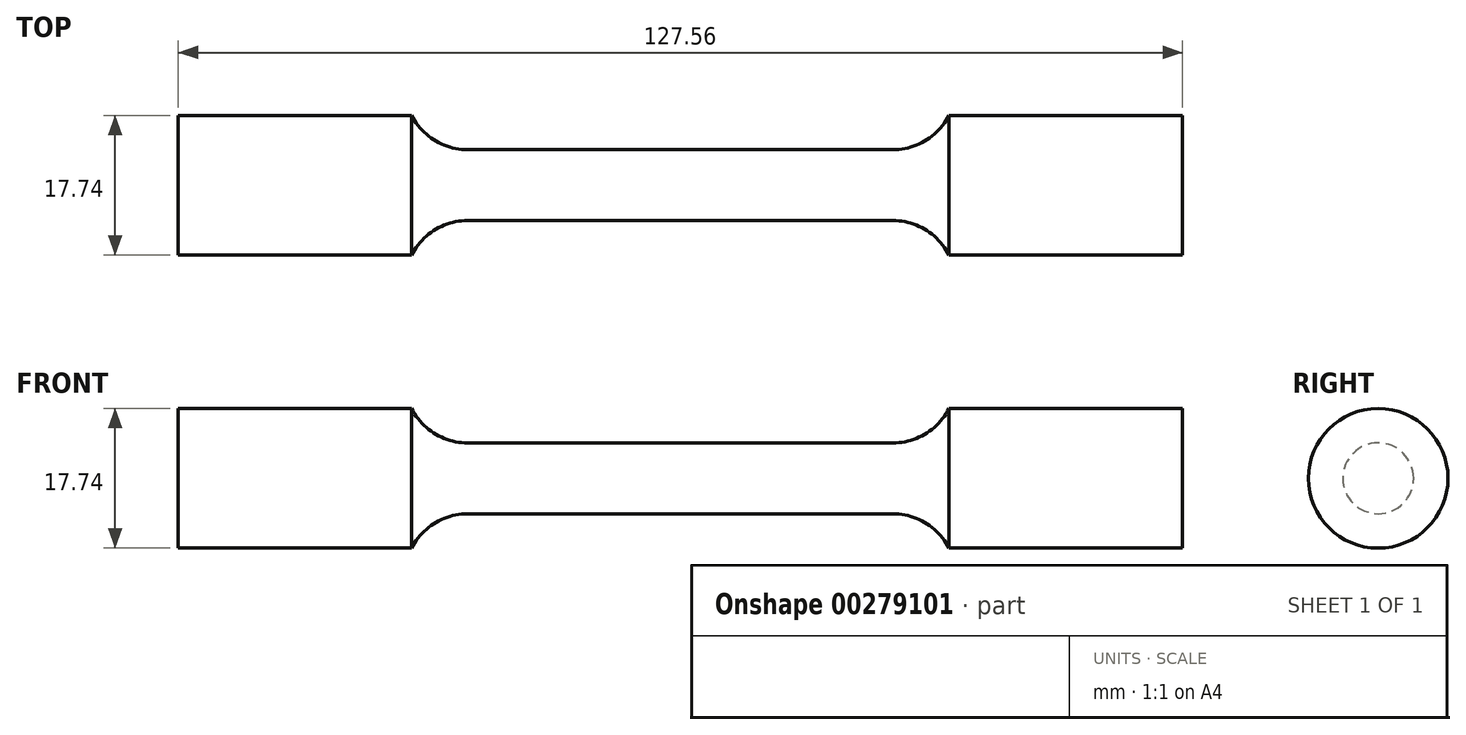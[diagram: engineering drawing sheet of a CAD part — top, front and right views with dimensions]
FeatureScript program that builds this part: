
annotation { "Feature Type Name" : "Feature", "Feature Type Description" : "" }
export const myFeature = defineFeature(function(context is Context, id is Id, definition is map)
    precondition{}
    {
        {
            var Q0;
            Q0=qCreatedBy(makeId("Front.planeOp"),FACE);
            var sketch = newSketch(context, id + "F0", { "sketchPlane" : qUnion([Q0])});
            skLineSegment(sketch, "E0", {"start": v(0, 4.5) * mm, "end": v(27, 4.5) * mm});
            skArc(sketch, "E1", {"start": v(27, 4.5) * mm, "mid": v(31.18, 5.68) * mm, "end": v(34.13, 8.87) * mm});
            skLineSegment(sketch, "E2", {"start": v(34.13, 8.87) * mm, "end": v(63.78, 8.87) * mm});
            skLineSegment(sketch, "E3", {"start": v(63.78, 8.87) * mm, "end": v(63.78, 0) * mm});
            skLineSegment(sketch, "E4.MirrorCS", {"start": v(0, 4.5) * mm, "end": v(-27, 4.5) * mm});
            skLineSegment(sketch, "E5.MirrorCS", {"start": v(-63.78, 8.87) * mm, "end": v(-63.78, 0) * mm});
            skLineSegment(sketch, "E6.MirrorCS", {"start": v(-34.13, 8.87) * mm, "end": v(-63.78, 8.87) * mm});
            skArc(sketch, "E7.MirrorCS", {"start": v(-27, 4.5) * mm, "mid": v(-31.18, 5.68) * mm, "end": v(-34.13, 8.87) * mm});
            skLineSegment(sketch, "E8", {"start": v(-63.78, 0) * mm, "end": v(63.78, 0) * mm});
            skLineSegment(sketch, "E9", {"start": v(-27, 4.5) * mm, "end": v(27, 4.5) * mm});
            skSolve(sketch);
        }
        {
            var Q0;
            Q0 = qSketchRegion(id + "F0", true);
            var Q1;
            Q1=sQuery(id+"F0.wireOp",EDGE,"E8");
            revolve(context, id + "F1", {"entities" : qUnion([Q0]), "axis" : qUnion([Q1]), "revolveType" : RevolveType.FULL});
        }
    });
